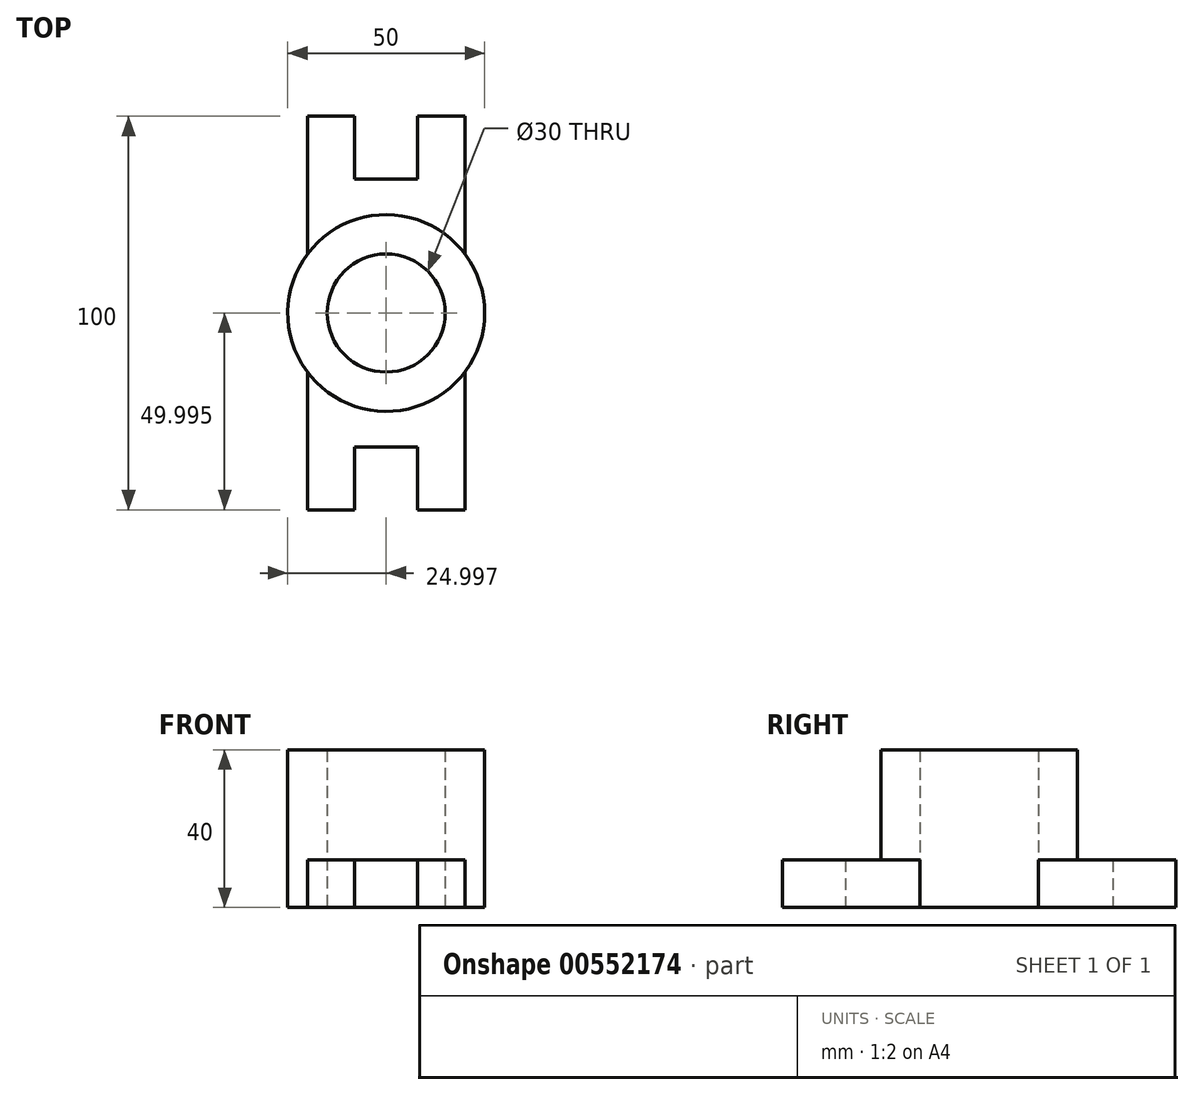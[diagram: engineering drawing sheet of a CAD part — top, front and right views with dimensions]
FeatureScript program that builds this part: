
annotation { "Feature Type Name" : "Feature", "Feature Type Description" : "" }
export const myFeature = defineFeature(function(context is Context, id is Id, definition is map)
    precondition{}
    {
        {
            var Q0;
            Q0=qCreatedBy(makeId("Top.planeOp"),FACE);
            var sketch = newSketch(context, id + "F0", { "sketchPlane" : qUnion([Q0])});
            skLineSegment(sketch, "E0.bottom", {"start": v(-23.64, -19.25) * mm, "end": v(-11.64, -19.25) * mm});
            skLineSegment(sketch, "E0.top", {"start": v(-23.64, 80.75) * mm, "end": v(-11.64, 80.75) * mm});
            skLineSegment(sketch, "E0.left", {"start": v(-23.64, -19.25) * mm, "end": v(-23.64, 15.75) * mm});
            skLineSegment(sketch, "E0.right", {"start": v(16.36, -19.25) * mm, "end": v(16.36, 15.75) * mm});
            skLineSegment(sketch, "E1.top", {"start": v(-11.64, -3.25) * mm, "end": v(4.36, -3.25) * mm});
            skLineSegment(sketch, "E1.left", {"start": v(-11.64, -19.25) * mm, "end": v(-11.64, -3.25) * mm});
            skLineSegment(sketch, "E1.right", {"start": v(4.36, -19.25) * mm, "end": v(4.36, -3.25) * mm});
            skLineSegment(sketch, "E2", {"start": v(-23.64, 30.75) * mm, "end": v(16.36, 30.75) * mm, "construction": true});
            skLineSegment(sketch, "E3.MirrorCS", {"start": v(-11.64, 80.75) * mm, "end": v(-11.64, 64.75) * mm});
            skLineSegment(sketch, "E4.MirrorCS", {"start": v(-11.64, 64.75) * mm, "end": v(4.36, 64.75) * mm});
            skLineSegment(sketch, "E5.MirrorCS", {"start": v(4.36, 80.75) * mm, "end": v(4.36, 64.75) * mm});
            skLineSegment(sketch, "E6.trimOffspring", {"start": v(4.36, 80.75) * mm, "end": v(16.36, 80.75) * mm});
            skLineSegment(sketch, "E7.trimOffspring", {"start": v(4.36, -19.25) * mm, "end": v(16.36, -19.25) * mm});
            skCircle(sketch, "E8", {"center": v(-3.64, 30.75) * mm, "radius": 25 * mm});
            skCircle(sketch, "E9", {"center": v(-3.64, 30.75) * mm, "radius": 15 * mm});
            skLineSegment(sketch, "E10.trimOffspring", {"start": v(-23.64, 45.75) * mm, "end": v(-23.64, 80.75) * mm});
            skLineSegment(sketch, "E11.trimOffspring", {"start": v(16.36, 45.75) * mm, "end": v(16.36, 80.75) * mm});
            skSolve(sketch);
        }
        {
            var Q0;
            Q0=makeQuery(id+"F0.imprint","IMPRINT",FACE,{"disambiguationData":[TD([[makeQuery(id+"F0.imprint","IMPRINT",EDGE,{"derivedFrom":sQuery(id+"F0.wireOp",EDGE,"E9")}),-1.0]])]});
            extrude(context, id + "F1", {"entities" : qUnion([Q0]), "depth" : 40 * mm, "offsetDistance" : 25 * mm});
        }
        {
            var Q0;
            Q0=makeQuery(id+"F0.imprint","IMPRINT",FACE,{"disambiguationData":[TD([[makeQuery(id+"F0.imprint","IMPRINT",EDGE,{"derivedFrom":sQuery(id+"F0.wireOp",EDGE,"E0.bottom")}),1.0]])]});
            var Q1;
            Q1=makeQuery(id+"F0.imprint","IMPRINT",FACE,{"disambiguationData":[TD([[makeQuery(id+"F0.imprint","IMPRINT",EDGE,{"derivedFrom":sQuery(id+"F0.wireOp",EDGE,"E0.top")}),-1.0]])]});
            extrude(context, id + "F2", {"entities" : qUnion([Q0, Q1]), "operationType" : NewBodyOperationType.ADD, "depth" : 12 * mm, "offsetDistance" : 25 * mm});
        }
    });
